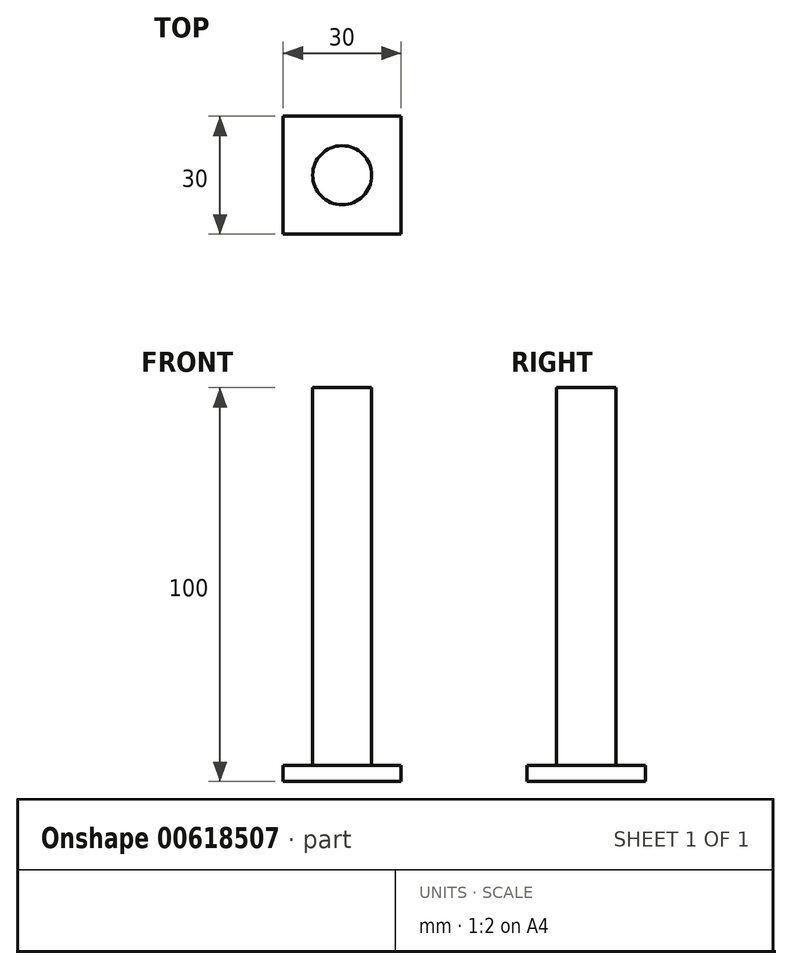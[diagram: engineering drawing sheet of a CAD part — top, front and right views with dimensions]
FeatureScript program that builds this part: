
annotation { "Feature Type Name" : "Feature", "Feature Type Description" : "" }
export const myFeature = defineFeature(function(context is Context, id is Id, definition is map)
    precondition{}
    {
        {
            var Q0;
            Q0=qCreatedBy(makeId("Top.planeOp"),FACE);
            var sketch = newSketch(context, id + "F0", { "sketchPlane" : qUnion([Q0])});
            skLineSegment(sketch, "E0.bottom", {"start": v(15, 15) * mm, "end": v(-15, 15) * mm});
            skLineSegment(sketch, "E0.top", {"start": v(15, -15) * mm, "end": v(-15, -15) * mm});
            skLineSegment(sketch, "E0.left", {"start": v(15, 15) * mm, "end": v(15, -15) * mm});
            skLineSegment(sketch, "E0.right", {"start": v(-15, 15) * mm, "end": v(-15, -15) * mm});
            skPoint(sketch, "E0.middle", {"position": v(0, 0) * mm});
            skSolve(sketch);
        }
        {
            var Q0;
            Q0=makeQuery(id+"F0.imprint","IMPRINT",FACE,{"disambiguationData":[TD([[makeQuery(id+"F0.imprint","IMPRINT",EDGE,{"derivedFrom":sQuery(id+"F0.wireOp",EDGE,"E0.bottom")}),1.0]])]});
            extrude(context, id + "F1", {"entities" : qUnion([Q0]), "depth" : 4 * mm, "offsetDistance" : 25 * mm});
        }
        {
            var Q0;
            Q0=makeQuery(id+"F1.opExtrude","CAP_FACE",FACE,{"disambiguationData":[OSD([sQuery(id+"F0.wireOp",EDGE,"E0.bottom"),sQuery(id+"F0.wireOp",EDGE,"E0.top"),sQuery(id+"F0.wireOp",EDGE,"E0.left"),sQuery(id+"F0.wireOp",EDGE,"E0.right")])],"isStart":false});
            var sketch = newSketch(context, id + "F2", { "sketchPlane" : qUnion([Q0])});
            skLineSegment(sketch, "E1", {"start": v(15, 15) * mm, "end": v(-15, -15) * mm, "construction": true});
            skCircle(sketch, "E2", {"center": v(0, 0) * mm, "radius": 7.5 * mm});
            skSolve(sketch);
        }
        {
            var Q0;
            Q0=makeQuery(id+"F2.imprint","IMPRINT",FACE,{"disambiguationData":[TD([[makeQuery(id+"F2.imprint","IMPRINT",EDGE,{"derivedFrom":sQuery(id+"F2.wireOp",EDGE,"E2")}),1.0]])]});
            extrude(context, id + "F3", {"entities" : qUnion([Q0]), "operationType" : NewBodyOperationType.ADD, "depth" : (100 - 4) * mm, "offsetDistance" : 25 * mm});
        }
    });
